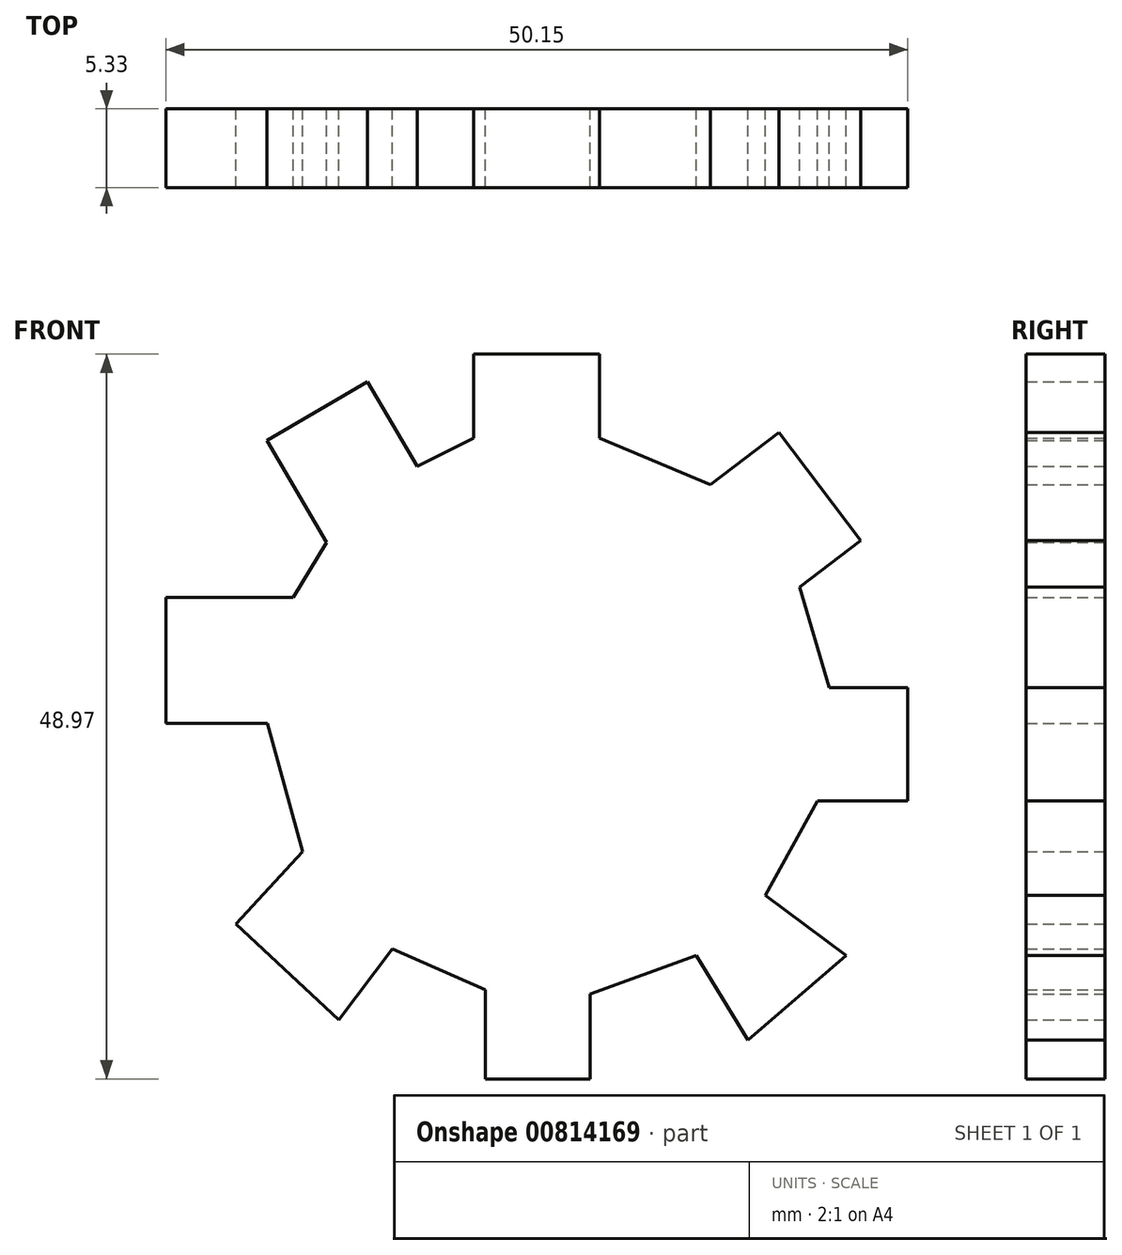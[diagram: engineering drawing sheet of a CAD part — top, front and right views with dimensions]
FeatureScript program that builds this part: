
annotation { "Feature Type Name" : "Feature", "Feature Type Description" : "" }
export const myFeature = defineFeature(function(context is Context, id is Id, definition is map)
    precondition{}
    {
        {
            var Q0;
            Q0=qCreatedBy(makeId("Front.planeOp"),FACE);
            var sketch = newSketch(context, id + "F0", { "sketchPlane" : qUnion([Q0])});
            skLineSegment(sketch, "E0.bottom", {"start": v(-29.58, 32.82) * mm, "end": v(-38.07, 32.82) * mm});
            skLineSegment(sketch, "E0.top", {"start": v(-29.58, 38.49) * mm, "end": v(-38.07, 38.49) * mm});
            skLineSegment(sketch, "E0.left", {"start": v(-29.58, 32.82) * mm, "end": v(-29.58, 38.49) * mm});
            skLineSegment(sketch, "E0.right", {"start": v(-38.07, 32.82) * mm, "end": v(-38.07, 38.49) * mm});
            skLineSegment(sketch, "E1", {"start": v(-22.07, 29.69) * mm, "end": v(-17.44, 33.2) * mm});
            skLineSegment(sketch, "E2", {"start": v(-17.44, 33.2) * mm, "end": v(-11.9, 25.88) * mm});
            skLineSegment(sketch, "E3", {"start": v(-11.9, 25.88) * mm, "end": v(-16.04, 22.75) * mm});
            skLineSegment(sketch, "E4", {"start": v(-14.04, 15.97) * mm, "end": v(-8.74, 15.97) * mm});
            skLineSegment(sketch, "E5", {"start": v(-8.74, 15.97) * mm, "end": v(-8.74, 8.31) * mm});
            skLineSegment(sketch, "E6", {"start": v(-8.74, 8.31) * mm, "end": v(-14.85, 8.31) * mm});
            skLineSegment(sketch, "E7", {"start": v(-18.36, 1.91) * mm, "end": v(-12.91, -2.13) * mm});
            skLineSegment(sketch, "E8", {"start": v(-12.91, -2.13) * mm, "end": v(-19.52, -7.87) * mm});
            skLineSegment(sketch, "E9", {"start": v(-19.52, -7.87) * mm, "end": v(-23.03, -2.13) * mm});
            skLineSegment(sketch, "E10", {"start": v(-30.2, -4.73) * mm, "end": v(-30.2, -10.48) * mm});
            skLineSegment(sketch, "E11", {"start": v(-30.2, -10.48) * mm, "end": v(-37.27, -10.48) * mm});
            skLineSegment(sketch, "E12", {"start": v(-37.27, -10.48) * mm, "end": v(-37.27, -4.45) * mm});
            skLineSegment(sketch, "E13", {"start": v(-43.59, -1.7) * mm, "end": v(-47.19, -6.48) * mm});
            skLineSegment(sketch, "E14", {"start": v(-47.19, -6.48) * mm, "end": v(-54.15, 0) * mm});
            skLineSegment(sketch, "E15", {"start": v(-54.15, 0) * mm, "end": v(-49.62, 4.86) * mm});
            skLineSegment(sketch, "E16", {"start": v(-52, 13.54) * mm, "end": v(-58.89, 13.54) * mm});
            skLineSegment(sketch, "E17", {"start": v(-58.89, 13.54) * mm, "end": v(-58.89, 22.06) * mm});
            skLineSegment(sketch, "E18", {"start": v(-58.89, 22.06) * mm, "end": v(-50.26, 22.06) * mm});
            skLineSegment(sketch, "E19", {"start": v(-48.01, 25.76) * mm, "end": v(-52.04, 32.67) * mm});
            skLineSegment(sketch, "E20", {"start": v(-52.04, 32.67) * mm, "end": v(-45.24, 36.64) * mm});
            skLineSegment(sketch, "E21", {"start": v(-45.24, 36.64) * mm, "end": v(-41.9, 30.9) * mm});
            skLineSegment(sketch, "E22", {"start": v(-41.9, 30.9) * mm, "end": v(-38.07, 32.82) * mm});
            skLineSegment(sketch, "E23", {"start": v(-29.58, 32.82) * mm, "end": v(-22.07, 29.69) * mm});
            skLineSegment(sketch, "E24", {"start": v(-16.04, 22.75) * mm, "end": v(-14.04, 15.97) * mm});
            skLineSegment(sketch, "E25", {"start": v(-14.85, 8.31) * mm, "end": v(-18.36, 1.91) * mm});
            skLineSegment(sketch, "E26", {"start": v(-23.03, -2.13) * mm, "end": v(-30.2, -4.73) * mm});
            skLineSegment(sketch, "E27", {"start": v(-37.27, -4.45) * mm, "end": v(-43.59, -1.7) * mm});
            skLineSegment(sketch, "E28", {"start": v(-49.62, 4.86) * mm, "end": v(-52, 13.54) * mm});
            skLineSegment(sketch, "E29", {"start": v(-50.26, 22.06) * mm, "end": v(-48.01, 25.76) * mm});
            skSolve(sketch);
        }
        {
            var Q0;
            Q0 = qSketchRegion(id + "F0", true);
            extrude(context, id + "F1", {"entities" : qUnion([Q0]), "depth" : 5.33 * mm, "offsetDistance" : 25.4 * mm});
        }
    });
